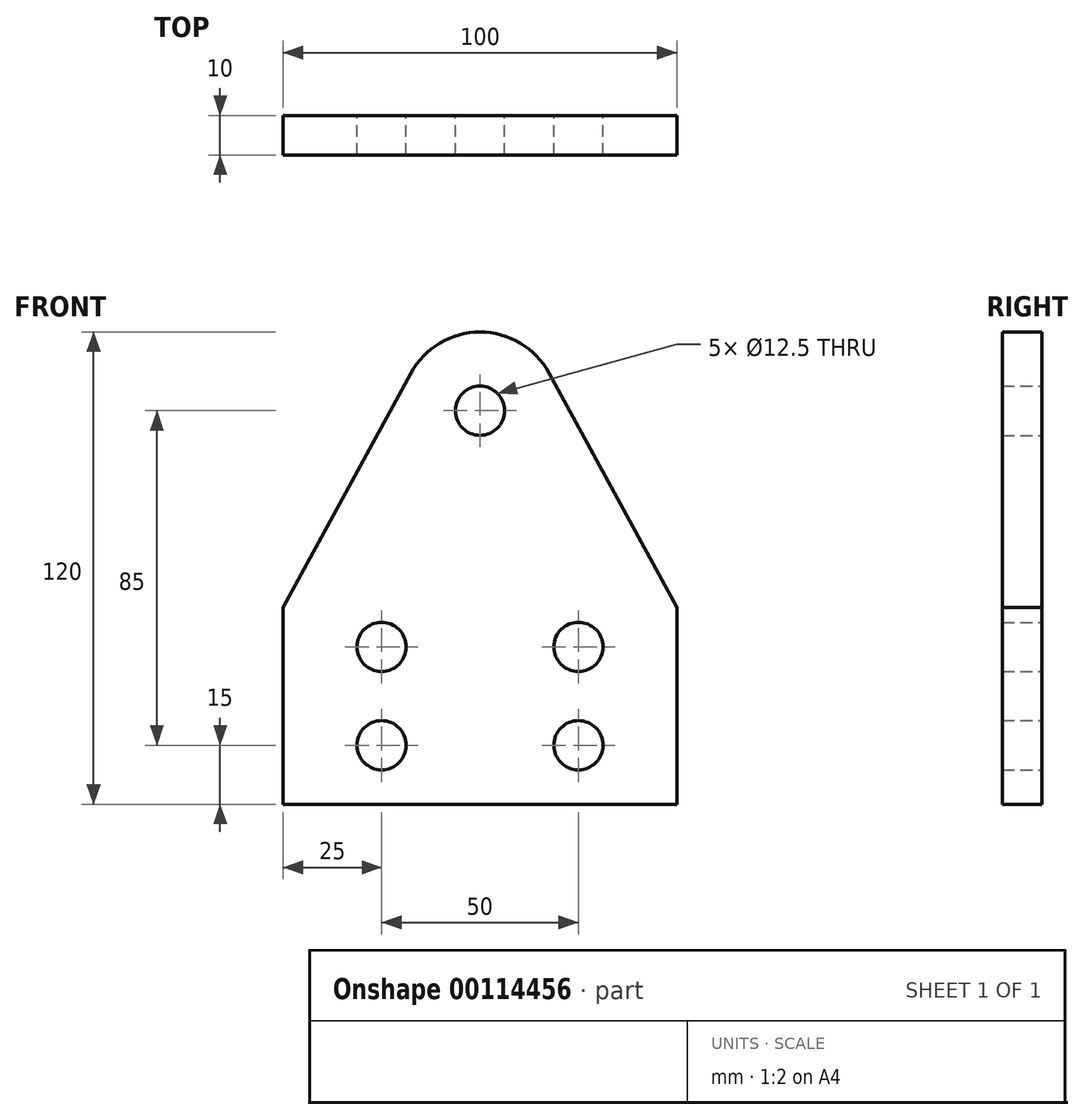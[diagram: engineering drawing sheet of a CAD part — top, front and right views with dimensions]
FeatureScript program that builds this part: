
annotation { "Feature Type Name" : "Feature", "Feature Type Description" : "" }
export const myFeature = defineFeature(function(context is Context, id is Id, definition is map)
    precondition{}
    {
        {
            var Q0;
            Q0=qCreatedBy(makeId("Front.planeOp"),FACE);
            var sketch = newSketch(context, id + "F0", { "sketchPlane" : qUnion([Q0])});
            skCircle(sketch, "E0", {"center": v(0, -8.64) * mm, "radius": 6.25 * mm});
            skArc(sketch, "E1", {"start": v(17.56, 0.92) * mm, "mid": v(0, 11.36) * mm, "end": v(-17.56, 0.92) * mm});
            skLineSegment(sketch, "E2", {"start": v(-50, -58.64) * mm, "end": v(-50, -108.64) * mm});
            skLineSegment(sketch, "E3", {"start": v(-50, -108.64) * mm, "end": v(0, -108.64) * mm});
            skLineSegment(sketch, "E4", {"start": v(-50, -58.64) * mm, "end": v(-17.56, 0.92) * mm});
            skLineSegment(sketch, "E5.MirrorCS", {"start": v(50, -108.64) * mm, "end": v(0, -108.64) * mm});
            skLineSegment(sketch, "E6.MirrorCS", {"start": v(50, -58.64) * mm, "end": v(17.56, 0.92) * mm});
            skLineSegment(sketch, "E7.MirrorCS", {"start": v(50, -58.64) * mm, "end": v(50, -108.64) * mm});
            skCircle(sketch, "E8", {"center": v(-25, -68.64) * mm, "radius": 6.25 * mm});
            skCircle(sketch, "E9", {"center": v(-25, -93.64) * mm, "radius": 6.25 * mm});
            skCircle(sketch, "E10.MirrorC", {"center": v(25, -68.64) * mm, "radius": 6.25 * mm});
            skCircle(sketch, "E11.MirrorC", {"center": v(25, -93.64) * mm, "radius": 6.25 * mm});
            skSolve(sketch);
        }
        {
            var Q0;
            Q0 = qSketchRegion(id + "F0", true);
            extrude(context, id + "F1", {"entities" : qUnion([Q0]), "depth" : 10 * mm});
        }
    });
